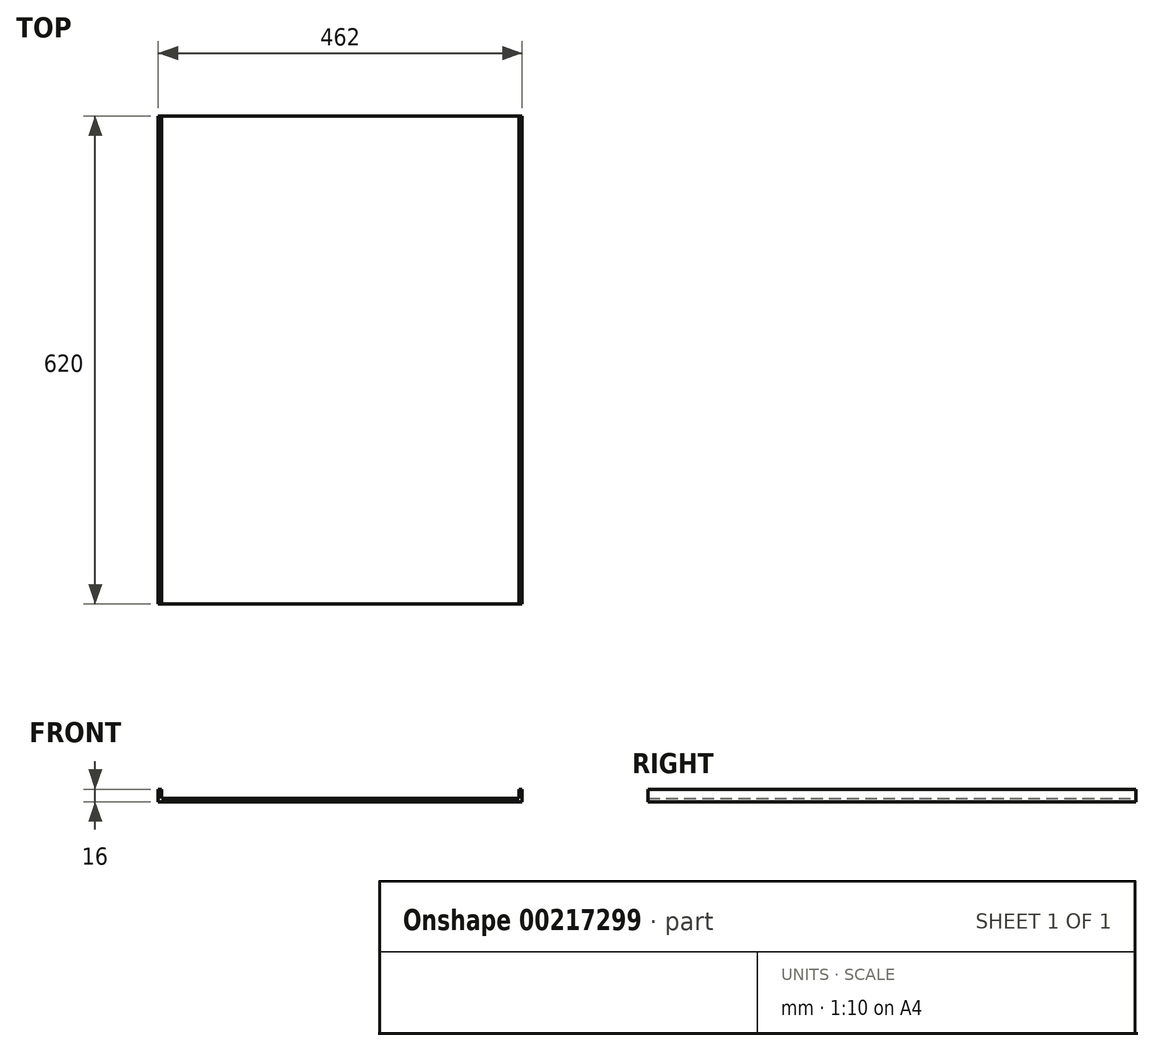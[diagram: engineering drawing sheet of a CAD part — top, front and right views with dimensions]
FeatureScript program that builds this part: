
annotation { "Feature Type Name" : "Feature", "Feature Type Description" : "" }
export const myFeature = defineFeature(function(context is Context, id is Id, definition is map)
    precondition{}
    {
        {
            var Q0;
            Q0=qCreatedBy(makeId("Top.planeOp"),FACE);
            var sketch = newSketch(context, id + "F0", { "sketchPlane" : qUnion([Q0])});
            skLineSegment(sketch, "E0.bottom", {"start": v(0, 0) * mm, "end": v(231, 0) * mm});
            skLineSegment(sketch, "E0.top", {"start": v(0, 310) * mm, "end": v(231, 310) * mm});
            skLineSegment(sketch, "E0.left", {"start": v(0, 0) * mm, "end": v(0, 310) * mm});
            skLineSegment(sketch, "E0.right", {"start": v(231, 0) * mm, "end": v(231, 310) * mm});
            skSolve(sketch);
        }
        {
            var Q0;
            Q0=makeQuery(id+"F0.imprint","IMPRINT",FACE,{"disambiguationData":[TD([[makeQuery(id+"F0.imprint","IMPRINT",EDGE,{"derivedFrom":sQuery(id+"F0.wireOp",EDGE,"E0.bottom")}),1.0]])]});
            extrude(context, id + "F1", {"entities" : qUnion([Q0]), "depth" : 4 * mm});
        }
        {
            var Q0;
            Q0=qCreatedBy(makeId("Right.planeOp"),FACE);
            var sketch = newSketch(context, id + "F2", { "sketchPlane" : qUnion([Q0])});
            skLineSegment(sketch, "E1.bottom", {"start": v(310, 0) * mm, "end": v(0, 0) * mm});
            skLineSegment(sketch, "E1.top", {"start": v(310, 16) * mm, "end": v(0, 16) * mm});
            skLineSegment(sketch, "E1.left", {"start": v(310, 0) * mm, "end": v(310, 16) * mm});
            skLineSegment(sketch, "E1.right", {"start": v(0, 0) * mm, "end": v(0, 16) * mm});
            skSolve(sketch);
        }
        {
            var Q0;
            Q0=makeQuery(id+"F2.imprint","IMPRINT",FACE,{"disambiguationData":[TD([[makeQuery(id+"F2.imprint","IMPRINT",EDGE,{"derivedFrom":sQuery(id+"F2.wireOp",EDGE,"E1.bottom")}),-1.0]])]});
            extrude(context, id + "F3", {"entities" : qUnion([Q0]), "operationType" : NewBodyOperationType.ADD, "depth" : 4 * mm});
        }
        {
            var Q0;
            Q0=makeQuery(id+"F1.opExtrude","SWEPT_BODY",BODY,{"disambiguationData":[OSD([sQuery(id+"F0.wireOp",EDGE,"E0.bottom"),sQuery(id+"F0.wireOp",EDGE,"E0.top"),sQuery(id+"F0.wireOp",EDGE,"E0.left"),sQuery(id+"F0.wireOp",EDGE,"E0.right")])]});
            var Q1;
            Q1=makeQuery(id+"F1.opExtrude","SWEPT_FACE",FACE,{"disambiguationData":[OSD([sQuery(id+"F0.wireOp",EDGE,"E0.right")])]});
            mirror(context, id + "F4", {"operationType" : NewBodyOperationType.ADD, "entities" : qUnion([Q0]), "mirrorPlane" : qUnion([Q1])});
        }
        {
            var Q0;
            Q0=makeQuery(id+"F1.opExtrude","SWEPT_BODY",BODY,{"disambiguationData":[OSD([sQuery(id+"F0.wireOp",EDGE,"E0.bottom"),sQuery(id+"F0.wireOp",EDGE,"E0.top"),sQuery(id+"F0.wireOp",EDGE,"E0.left"),sQuery(id+"F0.wireOp",EDGE,"E0.right")])]});
            var Q1;
            {var subQ0=makeQuery(id+"F3.boolean.opBoolean","MERGE",FACE,{"derivedFrom":[makeQuery(id+"F1.opExtrude","SWEPT_FACE",FACE,{"disambiguationData":[OSD([sQuery(id+"F0.wireOp",EDGE,"E0.bottom")])]}),makeQuery(id+"F3.opExtrude","SWEPT_FACE",FACE,{"disambiguationData":[OSD([sQuery(id+"F2.wireOp",EDGE,"E1.right")])]})]});Q1=makeQuery(id+"F4.boolean.opBoolean","MERGE",FACE,{"derivedFrom":[subQ0,makeQuery(id+"F4.opPattern","COPY",FACE,{"derivedFrom":subQ0,"instanceName":"1"})]});}
            mirror(context, id + "F5", {"operationType" : NewBodyOperationType.ADD, "entities" : qUnion([Q0]), "mirrorPlane" : qUnion([Q1])});
        }
    });
